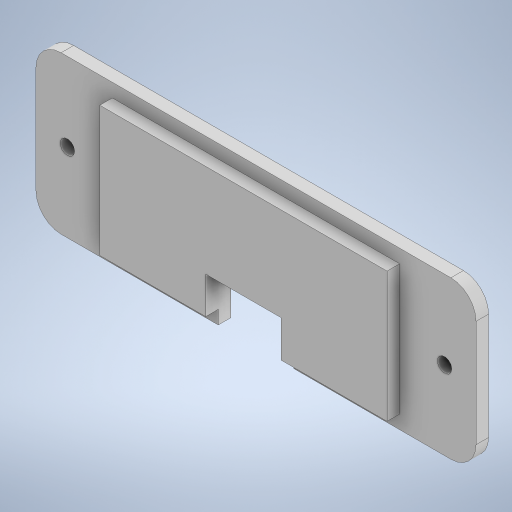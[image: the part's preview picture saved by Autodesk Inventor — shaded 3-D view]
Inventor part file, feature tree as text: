
AUTODESK INVENTOR PART (.ipt)
format: ipt  version: 2024.2 (Build 282272000, 272)  size: 281,088 bytes
history: native  units: mm
features: extrude x3, sketch x3, plane x1, fillet x1
ambient origin geometry x8: Origin, YZ Plane, XZ Plane, XY Plane, X Axis, Y Axis, Z Axis, Center Point
bodies: Solid1 (feature_tree)
feature tree (8):
  extrude  "Extrusion1"  Depth=25.0mm
  sketch  "Sketch4"  dims[d19=10.0mm d20=10.0mm]
  plane  "Work Plane1"
  sketch  "Sketch5"  dims[d21=2.3mm d22=2.3mm d25=20.7mm d26=2.15mm d27=45.7mm d32=12.0mm d33=8.0mm d36=4.0mm d37=12.5mm d38=12.5mm d39=12.5mm d40=5.0mm d41=5.0mm d42=12.5mm d43=12.5mm d44=12.15mm d45=2.0mm d46=0.0mm d50=29.0mm d51=0.0mm d52=0.0mm]
  fillet  "Fillet1"  Radius=2.0mm
  extrude  "Extrusion6"  Depth=10.0mm
  extrude  "Extrusion7"  Depth=29.0mm
  sketch  "Sketch1"  dims[d0=50.0mm d1=25.0mm d2=2.0mm d3=0.0mm]
